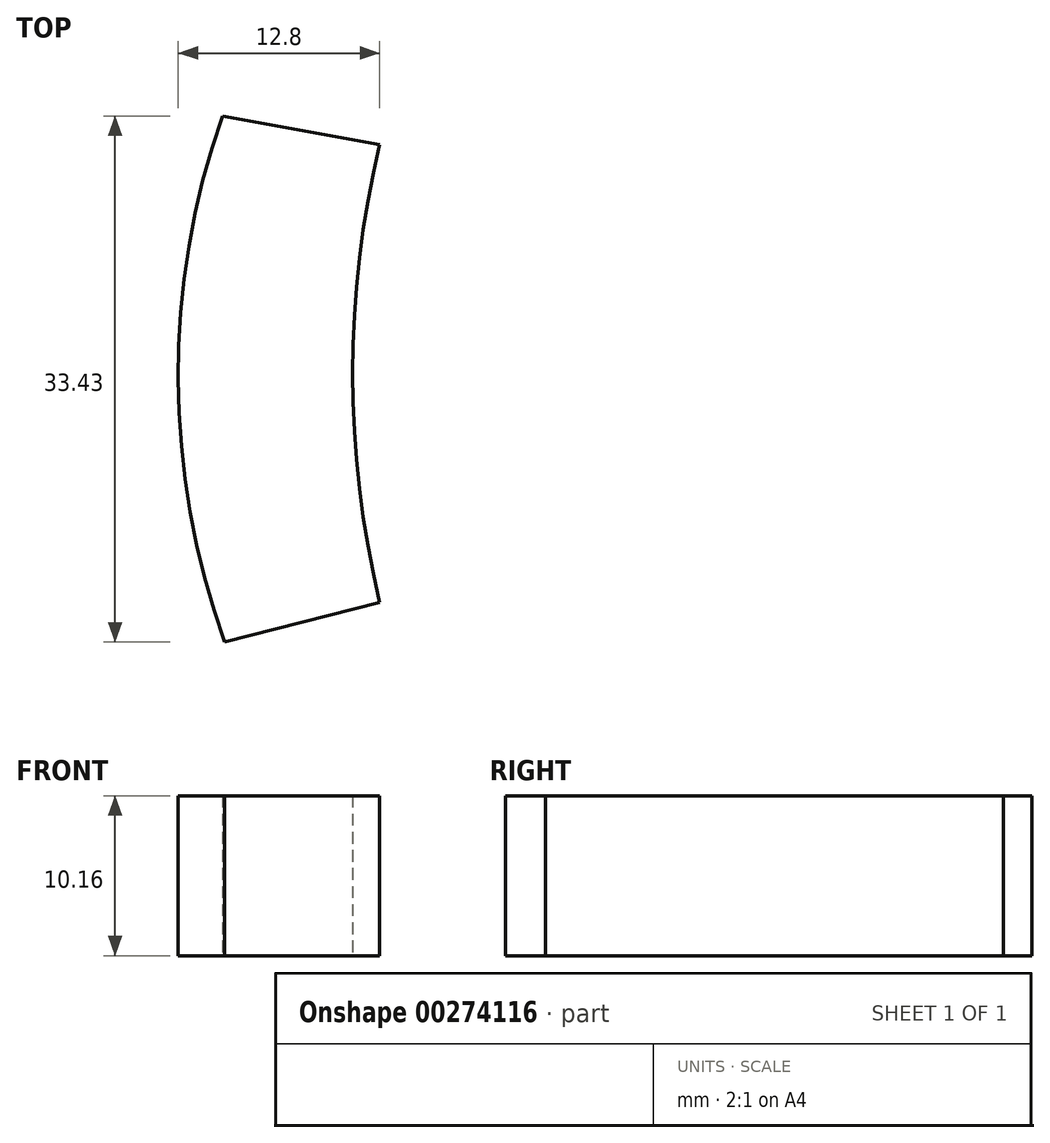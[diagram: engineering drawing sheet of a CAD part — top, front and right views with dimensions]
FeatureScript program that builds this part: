
annotation { "Feature Type Name" : "Feature", "Feature Type Description" : "" }
export const myFeature = defineFeature(function(context is Context, id is Id, definition is map)
    precondition{}
    {
        {
            var Q0;
            Q0=qCreatedBy(makeId("Top.planeOp"),FACE);
            var sketch = newSketch(context, id + "F0", { "sketchPlane" : qUnion([Q0])});
            skLineSegment(sketch, "E0", {"start": v(0, 4.01) * mm, "end": v(-9.84, 1.48) * mm});
            skLineSegment(sketch, "E1", {"start": v(0, 33.1) * mm, "end": v(-10, 34.9) * mm});
            skArc(sketch, "E2", {"start": v(-10, 34.9) * mm, "mid": v(-12.8, 18.18) * mm, "end": v(-9.84, 1.48) * mm});
            skArc(sketch, "E3", {"start": v(0, 33.1) * mm, "mid": v(-1.72, 18.55) * mm, "end": v(0, 4.01) * mm});
            skSolve(sketch);
        }
        {
            var Q0;
            Q0=makeQuery(id+"F0.imprint","IMPRINT",FACE,{"disambiguationData":[TD([[makeQuery(id+"F0.imprint","IMPRINT",EDGE,{"derivedFrom":sQuery(id+"F0.wireOp",EDGE,"E0")}),-1.0]])]});
            extrude(context, id + "F1", {"entities" : qUnion([Q0]), "depth" : 10.16 * mm});
        }
    });
